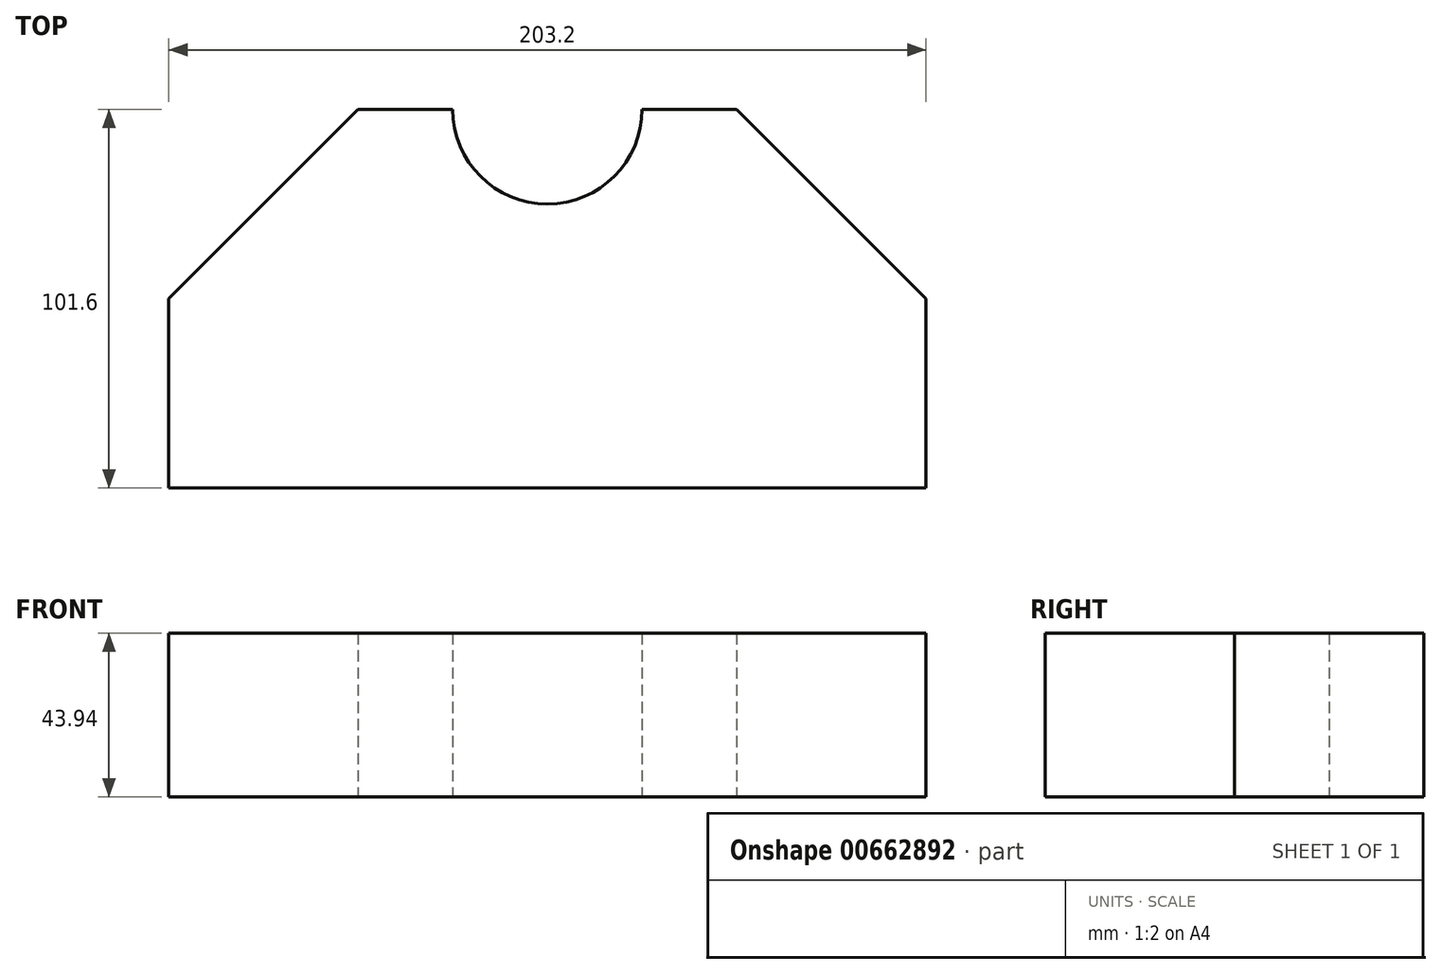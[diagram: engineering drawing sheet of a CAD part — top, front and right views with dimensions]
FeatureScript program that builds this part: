
annotation { "Feature Type Name" : "Feature", "Feature Type Description" : "" }
export const myFeature = defineFeature(function(context is Context, id is Id, definition is map)
    precondition{}
    {
        {
            var Q0;
            Q0=qCreatedBy(makeId("Top.planeOp"),FACE);
            var sketch = newSketch(context, id + "F0", { "sketchPlane" : qUnion([Q0])});
            skLineSegment(sketch, "E0", {"start": v(0, 0) * mm, "end": v(0, 50.8) * mm});
            skLineSegment(sketch, "E1", {"start": v(0, 50.8) * mm, "end": v(50.8, 101.6) * mm});
            skLineSegment(sketch, "E2", {"start": v(50.8, 101.6) * mm, "end": v(152.4, 101.6) * mm});
            skLineSegment(sketch, "E3", {"start": v(152.4, 101.6) * mm, "end": v(203.2, 50.8) * mm});
            skLineSegment(sketch, "E4", {"start": v(203.2, 50.8) * mm, "end": v(203.2, 0) * mm});
            skLineSegment(sketch, "E5", {"start": v(203.2, 0) * mm, "end": v(0, 0) * mm});
            skCircle(sketch, "E6", {"center": v(101.6, 101.6) * mm, "radius": 25.4 * mm});
            skSolve(sketch);
        }
        {
            var Q0;
            Q0=makeQuery(id+"F0.imprint","IMPRINT",FACE,{"disambiguationData":[TD([[makeQuery(id+"F0.imprint","IMPRINT",EDGE,{"derivedFrom":sQuery(id+"F0.wireOp",EDGE,"E0")}),-1.0]])]});
            var Q1;
            {var subQ0=sQuery(id+"F0.wireOp",EDGE,"E6");var subQ1=sQuery(id+"F0.wireOp",EDGE,"E2");var subQ2=makeQuery(id+"F0.imprint","INTERSECT",VERTEX,{"disambiguationData":[OD(0.0)],"derivedFrom":[subQ1,subQ0]});Q1=makeQuery(id+"F0.imprint","IMPRINT",FACE,{"disambiguationData":[TD([[makeQuery(id+"F0.imprint","IMPRINT",EDGE,{"disambiguationData":[TD([[subQ2,-1.0]])],"derivedFrom":subQ1}),1.0]])]});}
            var Q2;
            {var subQ0=sQuery(id+"F0.wireOp",EDGE,"E6");var subQ1=sQuery(id+"F0.wireOp",EDGE,"E2");var subQ2=makeQuery(id+"F0.imprint","INTERSECT",VERTEX,{"disambiguationData":[OD(0.0)],"derivedFrom":[subQ1,subQ0]});Q2=makeQuery(id+"F0.imprint","IMPRINT",FACE,{"disambiguationData":[TD([[makeQuery(id+"F0.imprint","IMPRINT",EDGE,{"disambiguationData":[TD([[subQ2,-1.0]])],"derivedFrom":subQ1}),-1.0]])]});}
            extrude(context, id + "F1", {"entities" : qUnion([Q0, Q1, Q2]), "depth" : 43.94 * mm, "offsetDistance" : 25.4 * mm});
        }
    });
